# Revit family: lgh-n150_200rxv2d-c_60Hz
name_source: partatom
category: 機械設備
units: mm (PartAtom-declared; Revit-internal decimal feet)

## family parameters
OmniClass タイトル = Heat Exchangers for Ventilation Air
OmniClass 番号 = 23.75.10.34.21
パーツ タイプ = 標準
ロード時にボイドで切り取り = いいえ
丸型コネクタ寸法 = 直径を使用
作業面ベース = いいえ
共有 = いいえ
常に垂直 = はい
部屋計算ポイント = はい

## types (2) — shared parameters
Box_D = 145  [stored 0.475722 ft]
Box_Depth = 175  [stored 0.574147 ft]
Box_H = 88  [stored 0.288714 ft]
Box_Height = 669  [stored 2.19488 ft]
Box_Width = 115  [stored 0.377297 ft]
Clearance Left = 600
Depth = 1144
Duct_Depth_OA_EA = 49  [stored 0.160761 ft]
Duct_Depth_SA_RA = 84  [stored 0.275591 ft]
Duct_Height = 202  [stored 0.66273 ft]
EAサイズ_D = 700  [stored 2.29659 ft]
EAサイズ_W = 270  [stored 0.885827 ft]
Height = 808  [stored 2.65092 ft]
IfcExportAs = IfcAirToAirHeatRecoveryType
IfcExportType = ROTARYWHEEL
OAサイズ_D = 700  [stored 2.29659 ft]
OAサイズ_W = 270  [stored 0.885827 ft]
OmniClassCode = 23-27 23 19 11
RAサイズ_D = 242  [stored 0.793963 ft]
SAサイズ_D = 242  [stored 0.793963 ft]
Sensor_D = 176  [stored 0.577428 ft]
Sensor_Depth = 115  [stored 0.377297 ft]
Sensor_H = 201  [stored 0.659449 ft]
Sensor_Height = 183
Sensor_Width = 184  [stored 0.603675 ft]
URL = https://www.mitsubishielectric.co.jp
Uniclass2015Code = Pr_60_60_36_88
Uniclass2015Title = Thermal wheels
Uniclass2015Version = Systems v1.9
ダクト幅 = 270 mm
ダクト径 = 250 mm
ダクト高 = 700 mm
メンテナンススペース = はい
仕様書バージョン = Version1.0
企業コード = 108420
分類コード = 50052504100070
初期抵抗 = 0.0 Pa
周波数 = 60 Hz
呼称 = 全熱交換ユニット
外気量 = 0.0 m³/h
天吊金具_幅 = 30  [stored 0.0984252 ft]
天吊金具_径 = 15  [stored 0.0492126 ft]
天吊金具_高さ = 404  [stored 1.32546 ft]
天吊金具ピッチ2 = 1015  [stored 3.33005 ft]
実風量 = 0.0 m³/h
形式 = 天井埋込ダクト形
排気量 = 0.0 m³/h
本体マテリアル = 溶融亜鉛めっき鋼板
極数 = 3
法定耐用年数 = 15
点検口 = はい
点検口_Depth = 450  [stored 1.47638 ft]
点検口離隔 = 150
点検口高さ = -808  [stored -2.65092 ft]
相 = 1
積算_科目 = 1 空気調和設備
符号 = HEU
製品リリース年月 = 2023/5/15
製品出荷対象 = 国内
製造元 = 三菱電機株式会社
設置方法 = 天井吊(隠ぺい)形
設計風量 = 0.0 m³/h
説明 = 業務用ロスナイ 天井埋込形 DCマイコン CO2センサー付
負荷分類 = 3_ファン類
運転質量 = 0.00 kg
電動機出力 = 0 W
電圧 = 200 V
zero-valued in all types: Clearance Bottom, Clearance Top

## per-type parameters (varying)
| type | Duct_Pitch | MAX静圧 | MAX風量 | MID静圧 | MID風量 | MIN静圧 | MIN風量 | SMAX静圧 | SMAX風量 | Width | エンタルピ交換効率_冷房 | エンタルピ交換効率_暖房 | 価格 | 天吊金具ピッチ1 | 機外静圧 | 機外静圧_排気 | 消費電力 | 温度交換効率 | 製品質量 | 質量 | 面風速 | 風量 | 騒音レベル(dB(A)) |
| LGH-N150RXV2D-C | 690  [stored 2.26378 ft] | 245.0 Pa | 1500.0 m³/h | 127.0 Pa | 1080.0 m³/h | 47.0 Pa | 660.0 m³/h | 275.0 Pa | 1500.0 m³/h | 1004  [stored 3.29396 ft] | 66.00% | 76.00% | 1363200 $ | 1057  [stored 3.46785 ft] | 275.0 Pa | 275.0 Pa | 900 W | 74.00% | 107.00 kg | 128.40 kg | 8.5 m/s | 1500.0 m³/h | 38.5 |
| LGH-N200RXV2D-C | 917  [stored 3.00853 ft] | 165.0 Pa | 2000.0 m³/h | 86.0 Pa | 1440.0 m³/h | 32.0 Pa | 880.0 m³/h | 225.0 Pa | 2000.0 m³/h | 1231  [stored 4.03871 ft] | 65.00% | 75.00% | 1523200 $ | 1284  [stored 4.2126 ft] | 225.0 Pa | 225.0 Pa | 1160 W | 73.00% | 117.00 kg | 140.40 kg | 11.3 m/s | 2000.0 m³/h | 41 |

note: column(s) folded — value = type name in every type: モデル

note: [stored X ft] marks values corroborated as IEEE doubles in the binary element streams (Revit-internal decimal feet)
